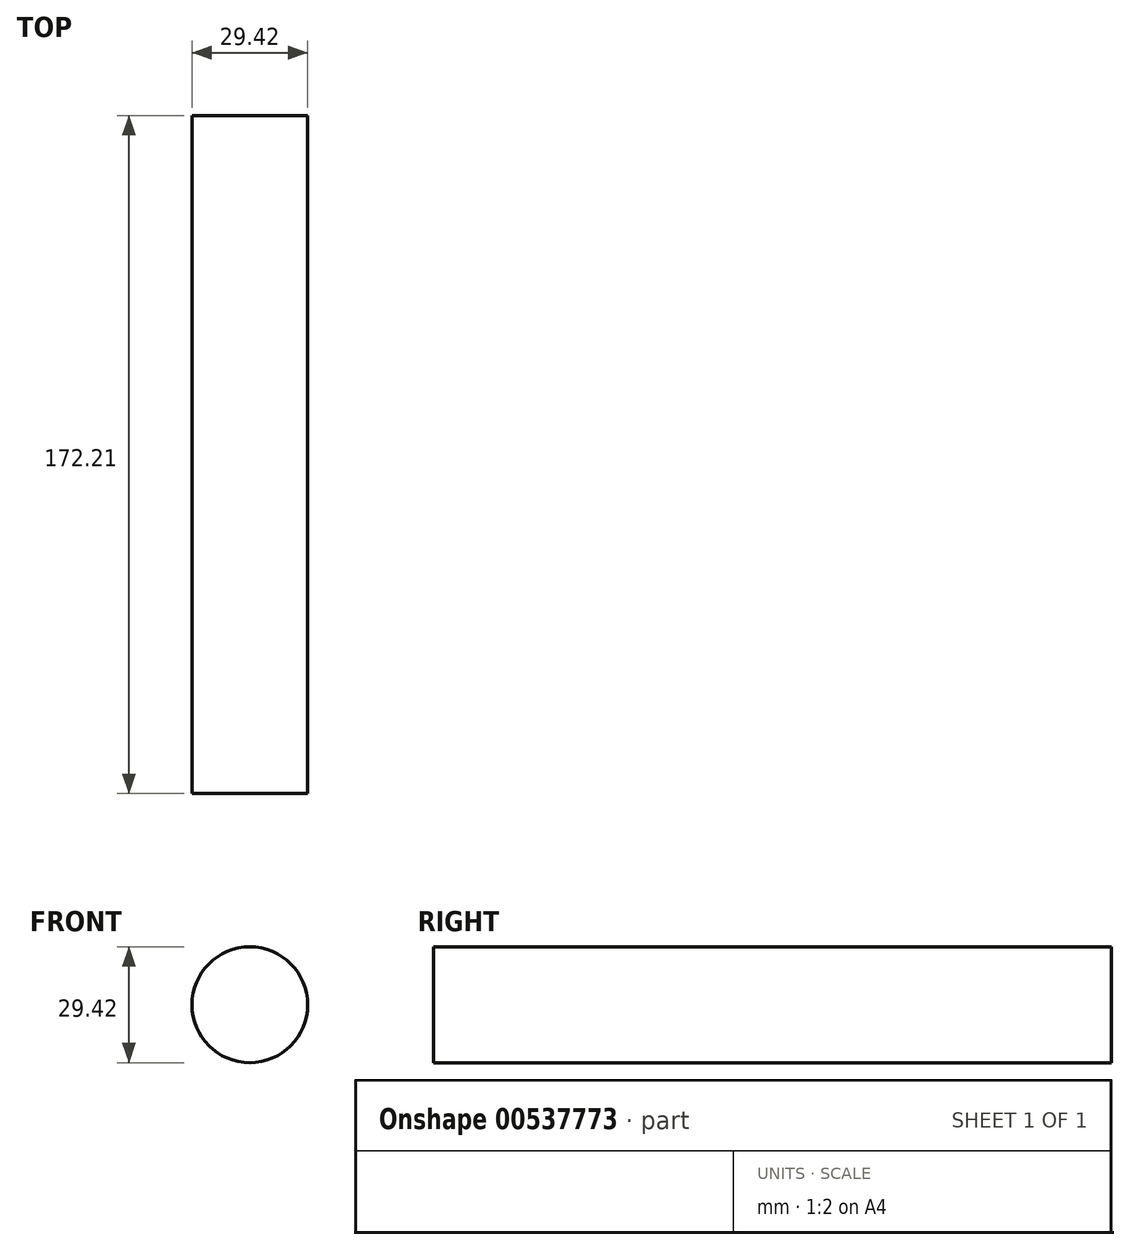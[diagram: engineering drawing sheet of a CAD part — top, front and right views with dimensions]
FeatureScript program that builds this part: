
annotation { "Feature Type Name" : "Feature", "Feature Type Description" : "" }
export const myFeature = defineFeature(function(context is Context, id is Id, definition is map)
    precondition{}
    {
        {
            var Q0;
            Q0=qCreatedBy(makeId("Front.planeOp"),FACE);
            var sketch = newSketch(context, id + "F0", { "sketchPlane" : qUnion([Q0])});
            skCircle(sketch, "E0", {"center": v(-6.42, 13.23) * mm, "radius": 14.71 * mm});
            skPoint(sketch, "E0.first.point", {"position": v(0, 0) * mm});
            skPoint(sketch, "E0.second.point", {"position": v(0, 26.47) * mm});
            skPoint(sketch, "E0.third.point", {"position": v(-20.75, 16.54) * mm});
            skSolve(sketch);
        }
        {
            var Q0;
            Q0 = qSketchRegion(id + "F0", true);
            extrude(context, id + "F1", {"entities" : qUnion([Q0]), "depth" : 172.21 * mm, "offsetDistance" : 25.4 * mm});
        }
    });
